# Revit family: Haworth_BuzziHub
name_source: partatom
category: Furniture
revit_build: Autodesk Revit 2018 (Build: 20170223_1515(x64)
units: mm (PartAtom-declared; Revit-internal decimal feet)

## family parameters
Always vertical = Yes
Cut with Voids When Loaded = No
OmniClass Number = 23.40.70.14.64.21
OmniClass Title = Systems Furniture
Room Calculation Point = No
Shared = No
Work Plane-Based = No

## types (3) — shared parameters
Actual Height = 100 "
Assembly Code = E2020200
Front Height = 100 "
Manufacturer = Haworth
Model = HCBZ-HBB
Revision Number = 1
Size = Verify Final Dim. w/ Haworth
URL = http://www.haworth.com
URL - Product = https://www.haworth.com
Warranty = http://www.haworth.com
zero-valued in all types: Booth Depth, Cushion Offset, Cushion Width

## per-type parameters (varying)
| type | Actual Depth | Actual Width | Booth Width | Description | Double | Side Control | Single | With Side | Without Side |
| HCBZ-HBB2 | 0 " | 100 " | 100 " | Haworth BuzziHub Double Booth | Yes | No | No | No | Yes |
| HCBZ-HBB1 | 0 " | 0 " | 0 " | Haworth BuzziHub Single Booth | No | No | Yes | No | Yes |
| HCBZ-HBB2-2 | 100 " | 100 " | 100 " | Haworth BuzziHub Double Booth w Side | Yes | Yes | No | Yes | No |

## geometry (parser evidence)
native form markers: Sweep x7
no freeform markers — native parametric forms only
